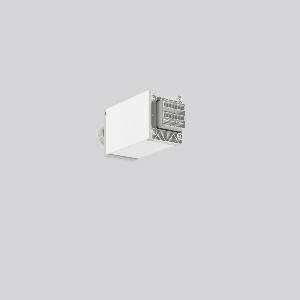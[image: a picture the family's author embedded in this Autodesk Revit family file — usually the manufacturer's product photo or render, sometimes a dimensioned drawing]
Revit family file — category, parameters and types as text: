
# Revit family: linedo_anfangseinspeisung_982859_002_1_2fe3
name_source: partatom
category: Lighting Fixtures
units: mm (PartAtom-declared; Revit-internal decimal feet)

## family parameters
Cut with Voids When Loaded = No
Host = Face
Light Source = No
Part Type = Normal
Room Calculation Point = No
Round Connector Dimension = Use Diameter
Shared = No

## types (1)
- LINEDO Anfangseinspeisung
    Apparent Load = 0 VA
    Default Elevation = 1800 mm
    Description = Series: LINEDO
Initial power feed (short Version), 7-pole, connection plug. Housing: extruded aluminium profile, powder-coated. Cover made of plastic, surface like housing. LINEDO plug system, plastic, light grey. 1 cable gland (M25). Cable gland on side or on top. Convenient connection with flat connector.
Colour: white
Length: 152 mm
Width: 58 mm
Height: 76 mm
Weight: 283 g
    Height = 76 mm
    Lamp = 0 x
    Length = 152 mm
    Luminous efficacy = 0 lm/W
    Manufacturer = RZB
    ModVariant = No
    Model = 982859.002.1
    Mounting Place = Ceiling
    Mounting Type = Surface mounted
    Number of Poles = 1
    OnlyDefault = Yes
    Power Factor = 1
    Product Name = LINEDO Anfangseinspeisung
    Product group = Continuous line luminaire system Linedo IP 54
    ProductGroupID = 314
    Protection Class = Protection class I
    Protection Degree = Degree of protection
    RLX_Detail_Level = 1
    RLX_Emergency_Light_Flux = 0 lm
    RLX_Emergency_Type = 0
    RLX_Emergency_Type_DB = No
    RlxData = <blob elided: 13073 chars, md5=6b4b5468>
    Standby Power = 0 W
    System Light Flux = 0 lm
    System Power = 0 W
    Type Comments = Product without accessories
    Type Image = 982859.002.1.jpg
    URL = http://relux.com
    VarID = ---
    Voltage = 0 V
    Weight = 0.00 kg
    Width = 58 mm

## geometry (parser evidence)
native form markers: Sweep x7
no freeform markers — native parametric forms only
